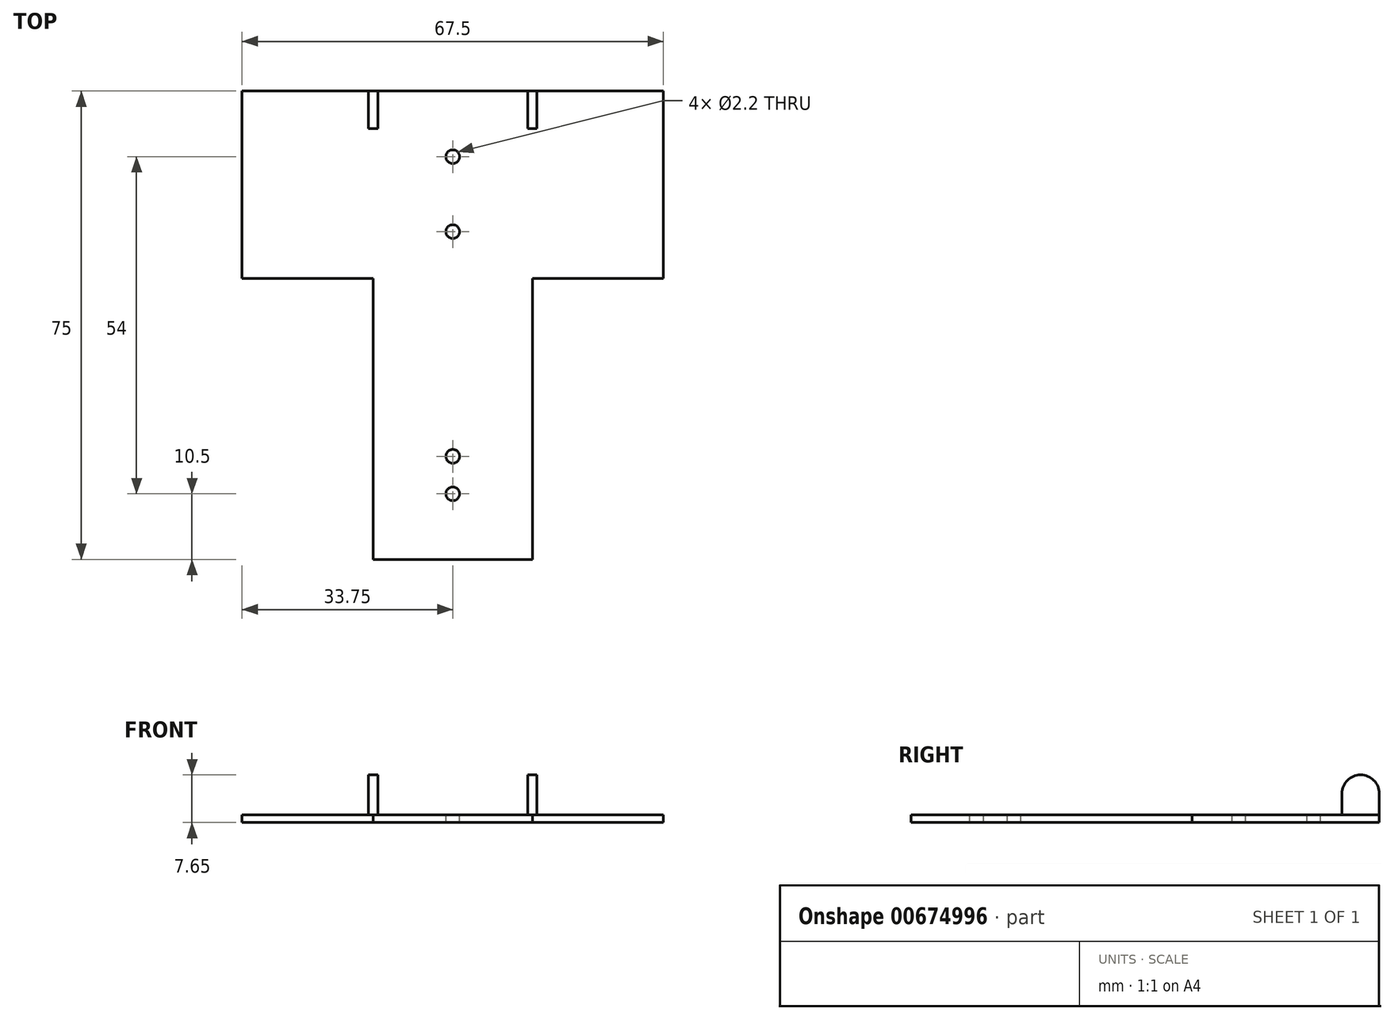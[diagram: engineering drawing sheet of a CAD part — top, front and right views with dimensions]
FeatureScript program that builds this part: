
annotation { "Feature Type Name" : "Feature", "Feature Type Description" : "" }
export const myFeature = defineFeature(function(context is Context, id is Id, definition is map)
    precondition{}
    {
        {
            assignVariable(context, id + "F0", {"name" : "Faktor", "anyValue" : 1.5});
        }
        {
            var Q0;
            Q0=qCreatedBy(makeId("Top.planeOp"),FACE);
            var sketch = newSketch(context, id + "F1", { "sketchPlane" : qUnion([Q0])});
            skLineSegment(sketch, "E0", {"start": v(-12.75, -27.5) * mm, "end": v(-12.75, 17.5) * mm});
            skLineSegment(sketch, "E1", {"start": v(-12.75, 17.5) * mm, "end": v(-33.75, 17.5) * mm});
            skLineSegment(sketch, "E2", {"start": v(-33.75, 17.5) * mm, "end": v(-33.75, 47.5) * mm});
            skLineSegment(sketch, "E3", {"start": v(-33.75, 47.5) * mm, "end": v(33.75, 47.5) * mm});
            skLineSegment(sketch, "E4", {"start": v(33.75, 47.5) * mm, "end": v(33.75, 17.5) * mm});
            skLineSegment(sketch, "E5", {"start": v(33.75, 17.5) * mm, "end": v(12.75, 17.5) * mm});
            skLineSegment(sketch, "E6", {"start": v(12.75, 17.5) * mm, "end": v(12.75, -27.5) * mm});
            skLineSegment(sketch, "E7", {"start": v(12.75, -27.5) * mm, "end": v(-12.75, -27.5) * mm});
            skSolve(sketch);
        }
        {
            var Q0;
            Q0=qSketchRegion(id+"F1",true);
            extrude(context, id + "F2", {"entities" : qUnion([Q0]), "depth" : getVariable(context, 'Faktor') * 0.8 * mm, "offsetDistance" : 25 * mm});
        }
        {
            var Q0;
            Q0=qCreatedBy(makeId("Right.planeOp"),FACE);
            cPlane(context, id + "F3", {"entities" : qUnion([Q0]), "cplaneType" : CPlaneType.OFFSET, "offset" : getVariable(context, 'Faktor') * 8 * mm, "width" : 150 * mm, "height" : 150 * mm});
        }
        {
            var Q0;
            Q0=qCreatedBy(id+"F3.planeOp",FACE);
            var sketch = newSketch(context, id + "F4", { "sketchPlane" : qUnion([Q0])});
            skLineSegment(sketch, "E8", {"start": v(41.5, 1.2) * mm, "end": v(41.5, 4.65) * mm});
            skLineSegment(sketch, "E9", {"start": v(41.5, 1.2) * mm, "end": v(47.5, 1.2) * mm});
            skLineSegment(sketch, "E10", {"start": v(47.5, 1.2) * mm, "end": v(47.5, 4.65) * mm});
            skLineSegment(sketch, "E11", {"start": v(-22.6, 4.65) * mm, "end": v(-28.17, 4.65) * mm, "construction": true});
            skArc(sketch, "E12", {"start": v(47.5, 4.65) * mm, "mid": v(44.5, 7.65) * mm, "end": v(41.5, 4.65) * mm});
            skSolve(sketch);
        }
        {
            var Q0;
            Q0=qSketchRegion(id+"F4",true);
            extrude(context, id + "F5", {"entities" : qUnion([Q0]), "depth" : getVariable(context, 'Faktor') * 1 * mm, "offsetDistance" : 25 * mm});
        }
        {
            var Q0;
            Q0=makeQuery(id+"F5.opExtrude","SWEPT_BODY",BODY,{"disambiguationData":[OSD([sQuery(id+"F4.wireOp",EDGE,"E8"),sQuery(id+"F4.wireOp",EDGE,"E9"),sQuery(id+"F4.wireOp",EDGE,"E10"),sQuery(id+"F4.wireOp",EDGE,"E12")])]});
            var Q1;
            Q1=qCreatedBy(makeId("Right.planeOp"),FACE);
            mirror(context, id + "F6", {"operationType" : NewBodyOperationType.ADD, "entities" : qUnion([Q0]), "mirrorPlane" : qUnion([Q1])});
        }
        {
            var Q0;
            Q0=makeQuery(id+"F2.opExtrude","CAP_FACE",FACE,{"disambiguationData":[OSD([sQuery(id+"F1.wireOp",EDGE,"E0"),sQuery(id+"F1.wireOp",EDGE,"E1"),sQuery(id+"F1.wireOp",EDGE,"E2"),sQuery(id+"F1.wireOp",EDGE,"E3"),sQuery(id+"F1.wireOp",EDGE,"E4"),sQuery(id+"F1.wireOp",EDGE,"E5"),sQuery(id+"F1.wireOp",EDGE,"E6"),sQuery(id+"F1.wireOp",EDGE,"E7")])],"isStart":false});
            var sketch = newSketch(context, id + "F7", { "sketchPlane" : qUnion([Q0])});
            skCircle(sketch, "E13", {"center": v(0, 37) * mm, "radius": 1.1 * mm});
            skCircle(sketch, "E14", {"center": v(0, 25) * mm, "radius": 1.1 * mm});
            skCircle(sketch, "E15", {"center": v(0, -11) * mm, "radius": 1.1 * mm});
            skCircle(sketch, "E16", {"center": v(0, -17) * mm, "radius": 1.1 * mm});
            skSolve(sketch);
        }
        {
            var Q0;
            Q0=qSketchRegion(id+"F7",true);
            extrude(context, id + "F8", {"entities" : qUnion([Q0]), "operationType" : NewBodyOperationType.REMOVE, "endBound" : BoundingType.THROUGH_ALL, "oppositeDirection" : true, "depth" : 25 * mm, "offsetDistance" : 25 * mm});
        }
    });
